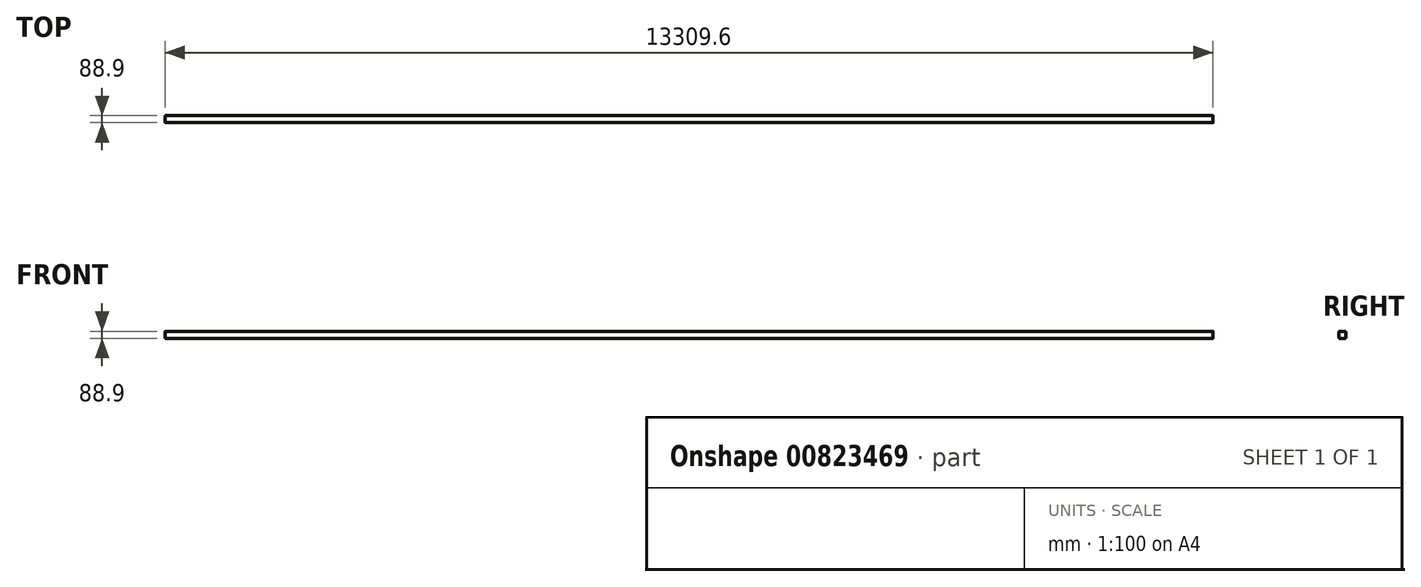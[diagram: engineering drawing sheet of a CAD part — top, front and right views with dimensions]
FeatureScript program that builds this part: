
annotation { "Feature Type Name" : "Feature", "Feature Type Description" : "" }
export const myFeature = defineFeature(function(context is Context, id is Id, definition is map)
    precondition{}
    {
        {
            var Q0;
            Q0=qCreatedBy(makeId("Right.planeOp"),FACE);
            var sketch = newSketch(context, id + "F0", { "sketchPlane" : qUnion([Q0])});
            skLineSegment(sketch, "E0.bottom", {"start": v(-38.1, 44.45) * mm, "end": v(38.1, 44.45) * mm});
            skLineSegment(sketch, "E0.top", {"start": v(-38.1, -44.45) * mm, "end": v(38.1, -44.45) * mm});
            skLineSegment(sketch, "E0.left", {"start": v(-44.45, 38.1) * mm, "end": v(-44.45, -38.1) * mm});
            skLineSegment(sketch, "E0.right", {"start": v(44.45, 38.1) * mm, "end": v(44.45, -38.1) * mm});
            skPoint(sketch, "E0.middle", {"position": v(0, 0) * mm});
            skPoint(sketch, "E1.visualSharp", {"position": v(44.45, 44.45) * mm});
            skArc(sketch, "E1.filletArc", {"start": v(44.45, 38.1) * mm, "mid": v(42.6, 42.6) * mm, "end": v(38.1, 44.45) * mm});
            skPoint(sketch, "E2.visualSharp", {"position": v(44.45, -44.45) * mm});
            skArc(sketch, "E2.filletArc", {"start": v(38.1, -44.45) * mm, "mid": v(42.6, -42.6) * mm, "end": v(44.45, -38.1) * mm});
            skPoint(sketch, "E3.visualSharp", {"position": v(-44.45, -44.45) * mm});
            skArc(sketch, "E3.filletArc", {"start": v(-44.45, -38.1) * mm, "mid": v(-42.6, -42.6) * mm, "end": v(-38.1, -44.45) * mm});
            skPoint(sketch, "E4.visualSharp", {"position": v(-44.45, 44.45) * mm});
            skArc(sketch, "E4.filletArc", {"start": v(-38.1, 44.45) * mm, "mid": v(-42.6, 42.6) * mm, "end": v(-44.45, 38.1) * mm});
            skSolve(sketch);
        }
        {
            var Q0;
            Q0 = qSketchRegion(id + "F0", true);
            extrude(context, id + "F1", {"entities" : qUnion([Q0]), "endBound" : BoundingType.SYMMETRIC, "depth" : 13309.6 * mm, "offsetDistance" : 25.4 * mm});
        }
    });
